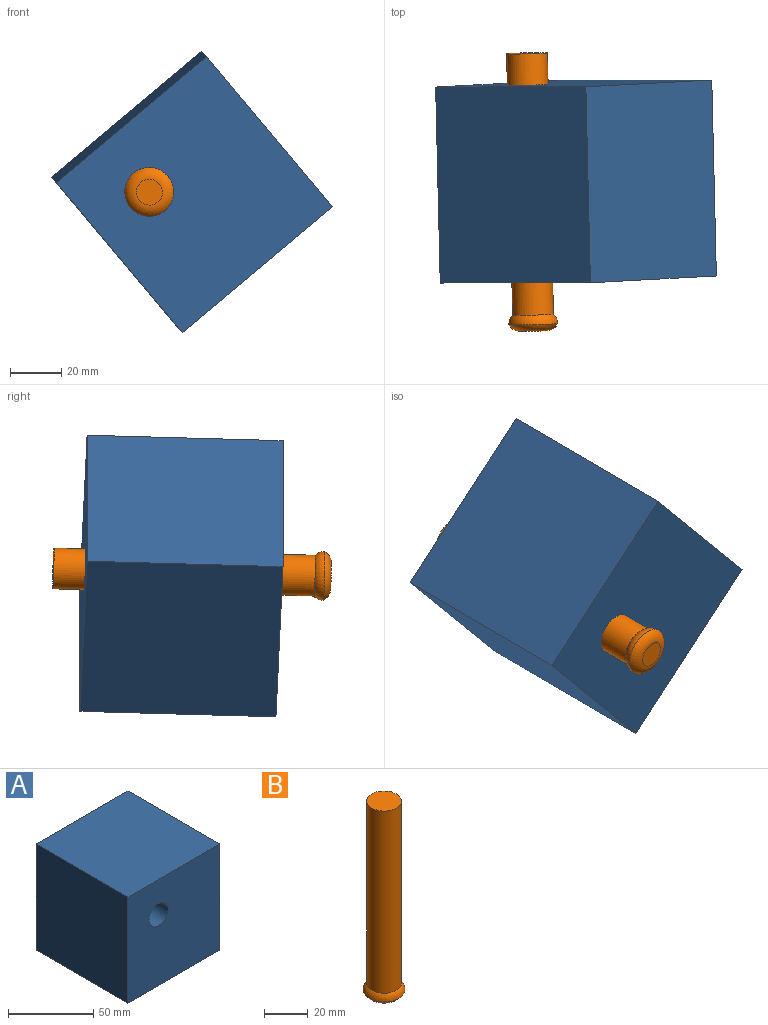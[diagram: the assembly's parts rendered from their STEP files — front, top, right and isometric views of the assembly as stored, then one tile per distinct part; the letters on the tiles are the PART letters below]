
ASSEMBLY  parts=2 mates=2
PART A: 7 faces, bbox 76.2x76.2x76.2 mm
  f0: plane 76.2x76.2mm, normal (0,0,1), area 5806.4mm2, adj f1,f3,f4,f5
  f1: plane 76.2x76.2mm, normal (-1,0,0), area 5806.4mm2, adj f0,f2,f4,f5
  f2: plane 76.2x76.2mm, normal (0,0,-1), area 5806.4mm2, adj f1,f3,f4,f5
  f3: plane 76.2x76.2mm, normal (1,0,0), area 5806.4mm2, adj f0,f2,f4,f5
  f4: plane 76.2x76.2mm, normal (0,-1,0), area 5608.5mm2, adj f0,f1,f2,f3,f6
  f5: plane 76.2x76.2mm, normal (0,1,0), area 5608.5mm2, adj f0,f1,f2,f3,f6
  f6: cylinder r=7.94mm len=76.2mm, axis (0,-1,0), area 3800.3mm2, adj f4,f5
PART B: 5 faces, bbox 19.1x19.1x108 mm
  f0: plane 10.12x10.12mm, normal (0,0,-1), area 80.4mm2, adj f4
  f1: cylinder r=7.94mm len=101.6mm, axis (0,0,-1), area 5067.1mm2, adj f2,f3
  f2: plane 15.88x15.88mm, normal (0,0,1), area 197.9mm2, adj f1
  f3: torus R=4.45mm, axis (0,0,1), area 233.1mm2, adj f1,f4
  f4: torus R=5.06mm, axis (0,0,-1), area 258.4mm2, adj f0,f3
PLACE A rot(axis=(0.05,-1,0.02),40.1deg) t=(-136.23,-140.96,66.54)mm
PLACE B rot(axis=(-0.25,0.67,0.7),152.5deg) t=(-150.76,-236.94,60.38)mm
MATE parallel A.f6 <-> B.f1  axis (0.02,-1,-0.03) through (-151.68,-217.68,70.44)mm
MATE slider A.f6 <-> B.f1  axis (-0.02,1,0.03) through (-153.46,-141.53,72.55)mm
